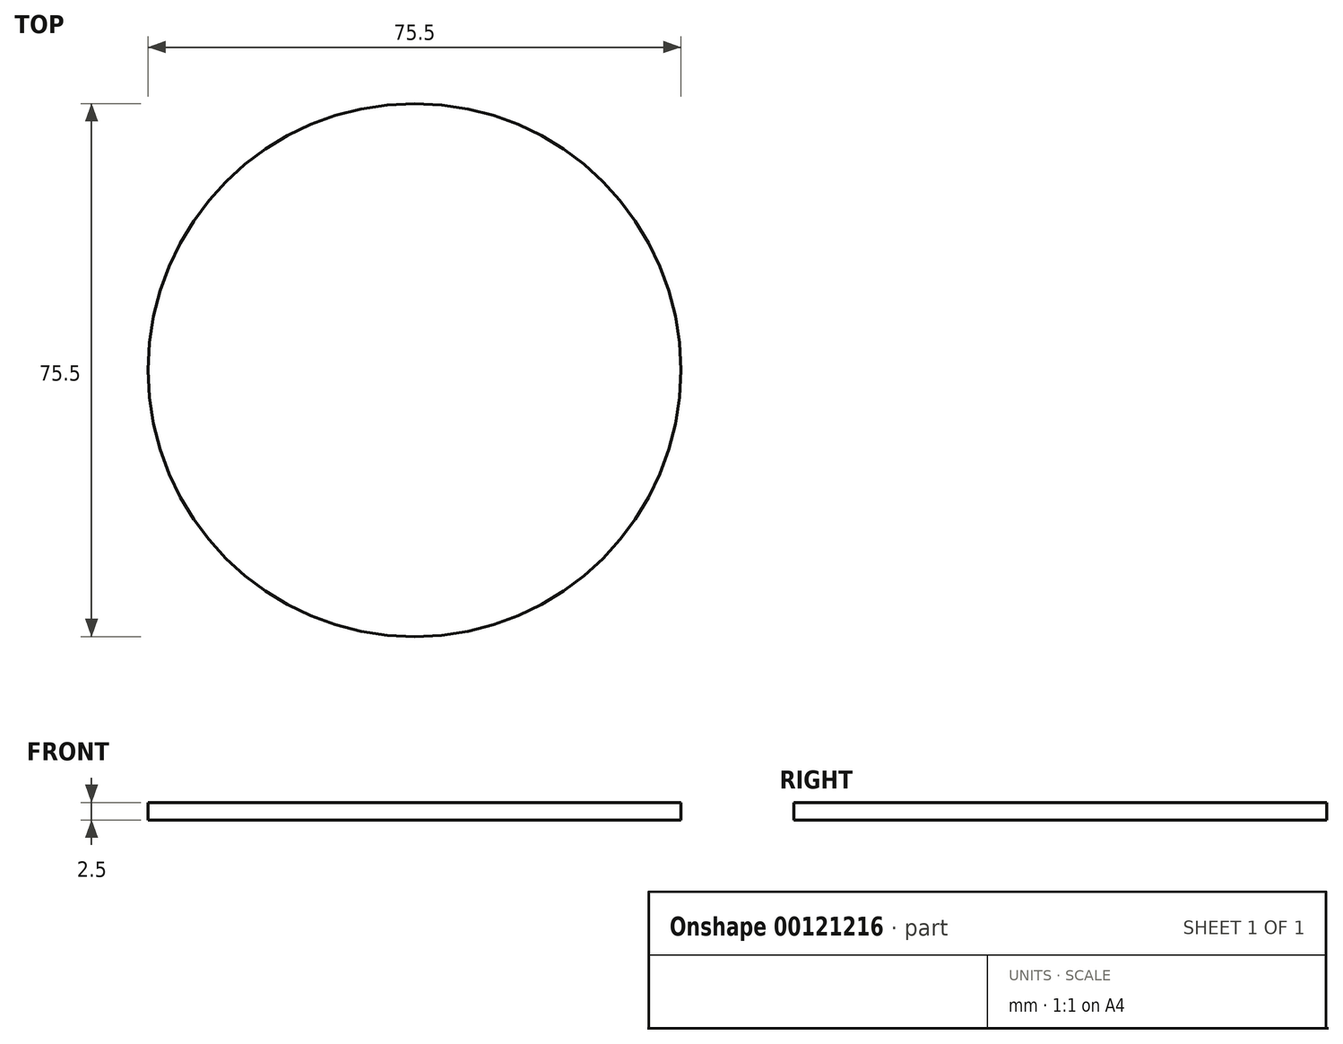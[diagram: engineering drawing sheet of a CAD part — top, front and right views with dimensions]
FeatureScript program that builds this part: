
annotation { "Feature Type Name" : "Feature", "Feature Type Description" : "" }
export const myFeature = defineFeature(function(context is Context, id is Id, definition is map)
    precondition{}
    {
        {
            var Q0;
            Q0=qCreatedBy(makeId("Top.planeOp"),FACE);
            var sketch = newSketch(context, id + "F0", { "sketchPlane" : qUnion([Q0])});
            skCircle(sketch, "E0", {"center": v(0, 0) * mm, "radius": 37.75 * mm});
            skSolve(sketch);
        }
        {
            var Q0;
            Q0 = qSketchRegion(id + "F0", true);
            extrude(context, id + "F1", {"entities" : qUnion([Q0]), "depth" : 2.5 * mm});
        }
    });
